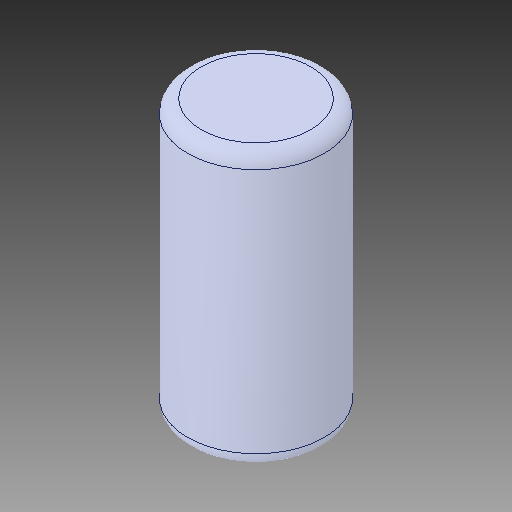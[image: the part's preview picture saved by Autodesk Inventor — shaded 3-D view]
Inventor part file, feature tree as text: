
AUTODESK INVENTOR PART (.ipt)
format: ipt  version: 2019 (Build 230136000, 136)  size: 117,760 bytes
history: native  units: in
note: dims shown in document units (in); Inventor stores cm internally (conversion verified against a paired STEP export)
features: fillet x1
ambient origin geometry x8: Origin, YZ Plane, XZ Plane, XY Plane, X Axis, Y Axis, Z Axis, Center Point
bodies: Solid1 (feature_tree)
feature tree (1):
  fillet  "Fillet1"  [1 undecoded]
note: 1 required parameter value undecoded (feature->parameter linkage not recoverable at this tier; creation-order binding heuristic only, values carry confidence <= 0.55)
